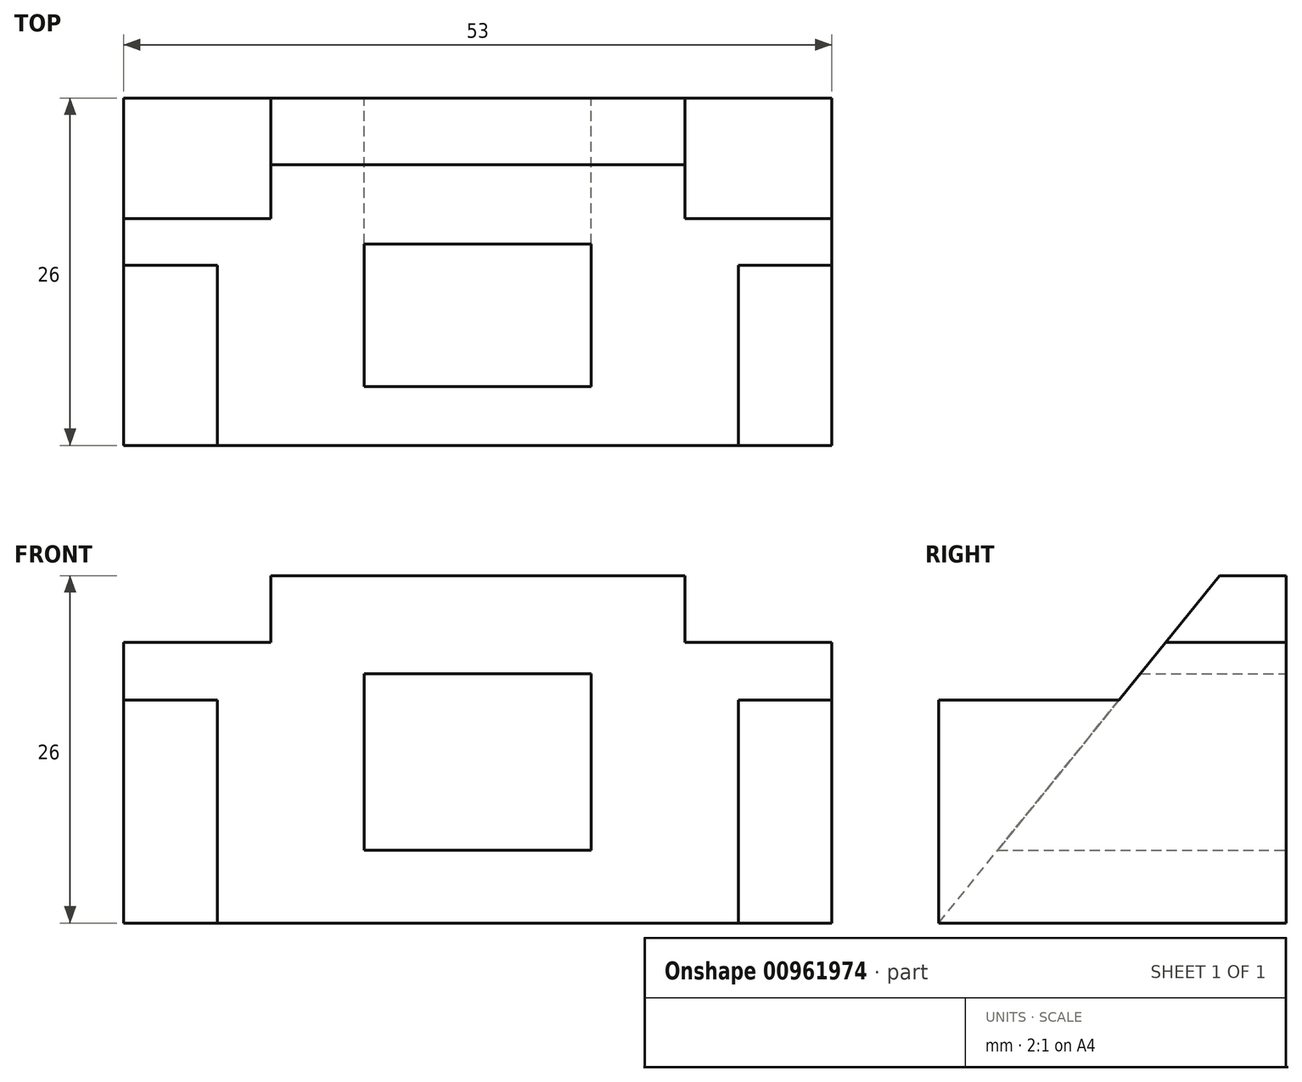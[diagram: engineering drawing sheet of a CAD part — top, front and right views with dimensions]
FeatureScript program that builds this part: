
annotation { "Feature Type Name" : "Feature", "Feature Type Description" : "" }
export const myFeature = defineFeature(function(context is Context, id is Id, definition is map)
    precondition{}
    {
        {
            var Q0;
            Q0=qCreatedBy(makeId("Top.planeOp"),FACE);
            var sketch = newSketch(context, id + "F0", { "sketchPlane" : qUnion([Q0])});
            skLineSegment(sketch, "E0.bottom", {"start": v(0, 0) * mm, "end": v(53, 0) * mm});
            skLineSegment(sketch, "E0.top", {"start": v(0, 26) * mm, "end": v(53, 26) * mm});
            skLineSegment(sketch, "E0.left", {"start": v(0, 0) * mm, "end": v(0, 26) * mm});
            skLineSegment(sketch, "E0.right", {"start": v(53, 0) * mm, "end": v(53, 26) * mm});
            skSolve(sketch);
        }
        {
            var Q0;
            Q0=makeQuery(id+"F0.imprint","IMPRINT",FACE,{"disambiguationData":[TD([[makeQuery(id+"F0.imprint","IMPRINT",EDGE,{"derivedFrom":sQuery(id+"F0.wireOp",EDGE,"E0.bottom")}),1.0]])]});
            extrude(context, id + "F1", {"entities" : qUnion([Q0]), "depth" : 26 * mm, "offsetDistance" : 25 * mm});
        }
        {
            var Q0;
            Q0=makeQuery(id+"F1.opExtrude","SWEPT_FACE",FACE,{"disambiguationData":[OSD([sQuery(id+"F0.wireOp",EDGE,"E0.right")])]});
            cPlane(context, id + "F2", {"entities" : qUnion([Q0]), "cplaneType" : CPlaneType.OFFSET, "offset" : 7 * mm, "oppositeDirection" : true, "width" : 150 * mm, "height" : 150 * mm});
        }
        {
            var Q0;
            Q0=qCreatedBy(id+"F2.planeOp",FACE);
            var sketch = newSketch(context, id + "F3", { "sketchPlane" : qUnion([Q0])});
            skLineSegment(sketch, "E1.0", {"start": v(0, 26) * mm, "end": v(26, 26) * mm});
            skPoint(sketch, "E2.0", {"position": v(0, 0) * mm});
            skLineSegment(sketch, "E3", {"start": v(0, 0) * mm, "end": v(21, 26) * mm});
            skLineSegment(sketch, "E4", {"start": v(0, 26) * mm, "end": v(0, 0) * mm});
            skSolve(sketch);
        }
        {
            var Q0;
            Q0 = qSketchRegion(id + "F3", true);
            extrude(context, id + "F4", {"entities" : qUnion([Q0]), "operationType" : NewBodyOperationType.REMOVE, "oppositeDirection" : true, "depth" : 39 * mm, "offsetDistance" : 25 * mm});
        }
        {
            var Q0;
            Q0=makeQuery(id+"F1.opExtrude","SWEPT_FACE",FACE,{"disambiguationData":[OSD([sQuery(id+"F0.wireOp",EDGE,"E0.right")])]});
            var sketch = newSketch(context, id + "F5", { "sketchPlane" : qUnion([Q0])});
            skLineSegment(sketch, "E5.0", {"start": v(0, 26) * mm, "end": v(26, 26) * mm});
            skLineSegment(sketch, "E6.0", {"start": v(26, 26) * mm, "end": v(26, 0) * mm});
            skLineSegment(sketch, "E7.0", {"start": v(0, 0) * mm, "end": v(26, 0) * mm});
            skLineSegment(sketch, "E8.0", {"start": v(0, 26) * mm, "end": v(0, 0) * mm});
            skLineSegment(sketch, "E9", {"start": v(26, 21) * mm, "end": v(16.96, 21) * mm});
            skLineSegment(sketch, "E10", {"start": v(13.49, 16.7) * mm, "end": v(0, 16.7) * mm});
            skLineSegment(sketch, "E11.0", {"start": v(13.49, 16.7) * mm, "end": v(16.96, 21) * mm});
            skPoint(sketch, "E12.orphan", {"position": v(21, 26) * mm});
            skPoint(sketch, "E13.orphan", {"position": v(0, 0) * mm});
            skSolve(sketch);
        }
        {
            var Q0;
            {var subQ1=sQuery(id+"F5.wireOp",EDGE,"E5.0");Q0=makeQuery(id+"F5.imprint","IMPRINT",FACE,{"disambiguationData":[TD([[makeQuery(id+"F5.imprint","IMPRINT",EDGE,{"derivedFrom":subQ1}),-1.0]])]});}
            extrude(context, id + "F6", {"entities" : qUnion([Q0]), "operationType" : NewBodyOperationType.REMOVE, "oppositeDirection" : true, "depth" : 11 * mm, "offsetDistance" : 25 * mm});
        }
        {
            var Q0;
            Q0=makeQuery(id+"F1.opExtrude","SWEPT_FACE",FACE,{"disambiguationData":[OSD([sQuery(id+"F0.wireOp",EDGE,"E0.left")])]});
            var sketch = newSketch(context, id + "F7", { "sketchPlane" : qUnion([Q0])});
            skLineSegment(sketch, "E14.0.0", {"start": v(-16.96, 21) * mm, "end": v(-13.49, 16.7) * mm});
            skLineSegment(sketch, "E14.0.1", {"start": v(-13.49, 16.7) * mm, "end": v(0, 16.7) * mm});
            skLineSegment(sketch, "E14.0.2", {"start": v(0, 16.7) * mm, "end": v(0, 0) * mm});
            skLineSegment(sketch, "E14.0.3", {"start": v(0, 0) * mm, "end": v(-26, 0) * mm});
            skLineSegment(sketch, "E14.0.4", {"start": v(-26, 0) * mm, "end": v(-26, 21) * mm});
            skLineSegment(sketch, "E14.0.5", {"start": v(-26, 21) * mm, "end": v(-16.96, 21) * mm});
            skLineSegment(sketch, "E15.0", {"start": v(-26, 26) * mm, "end": v(-26, 0) * mm});
            skLineSegment(sketch, "E16.0", {"start": v(0, 26) * mm, "end": v(-26, 26) * mm});
            skLineSegment(sketch, "E17.0", {"start": v(0, 26) * mm, "end": v(0, 0) * mm});
            skSolve(sketch);
        }
        {
            var Q0;
            Q0=makeQuery(id+"F7.imprint","IMPRINT",FACE,{"disambiguationData":[TD([[makeQuery(id+"F7.imprint","IMPRINT",EDGE,{"derivedFrom":sQuery(id+"F7.wireOp",EDGE,"E14.0.0")}),1.0]])]});
            extrude(context, id + "F8", {"entities" : qUnion([Q0]), "operationType" : NewBodyOperationType.REMOVE, "oppositeDirection" : true, "depth" : 11 * mm, "offsetDistance" : 25 * mm});
        }
        {
            var Q0;
            Q0=makeQuery(id+"F8.boolean.opBoolean","MERGE",FACE,{"derivedFrom":[makeQuery(id+"F6.boolean.opBoolean","MERGE",FACE,{"derivedFrom":[makeQuery(id+"F4.boolean.opBoolean","COPY",FACE,{"derivedFrom":makeQuery(id+"F4.opExtrude","SWEPT_FACE",FACE,{"disambiguationData":[OSD([sQuery(id+"F3.wireOp",EDGE,"E3")])]})})],"fromTools":[makeQuery(id+"F6.opExtrude","SWEPT_FACE",FACE,{"disambiguationData":[OSD([sQuery(id+"F5.wireOp",EDGE,"E11.0")])]})]})],"fromTools":[makeQuery(id+"F8.opExtrude","SWEPT_FACE",FACE,{"disambiguationData":[OSD([sQuery(id+"F7.wireOp",EDGE,"E14.0.0")])]})]});
            var sketch = newSketch(context, id + "F9", { "sketchPlane" : qUnion([Q0])});
            skLineSegment(sketch, "E18.bottom", {"start": v(18, 24) * mm, "end": v(35, 24) * mm});
            skLineSegment(sketch, "E18.top", {"start": v(18, 7) * mm, "end": v(35, 7) * mm});
            skLineSegment(sketch, "E18.left", {"start": v(18, 24) * mm, "end": v(18, 7) * mm});
            skLineSegment(sketch, "E18.right", {"start": v(35, 24) * mm, "end": v(35, 7) * mm});
            skSolve(sketch);
        }
        {
            var Q0;
            Q0=makeQuery(id+"F1.opExtrude","SWEPT_FACE",FACE,{"disambiguationData":[OSD([sQuery(id+"F0.wireOp",EDGE,"E0.top")])]});
            var sketch = newSketch(context, id + "F10", { "sketchPlane" : qUnion([Q0])});
            skLineSegment(sketch, "E19.0", {"start": v(-18, 18.67) * mm, "end": v(-35, 18.67) * mm});
            skLineSegment(sketch, "E20.0", {"start": v(-18, 18.67) * mm, "end": v(-18, 5.45) * mm});
            skLineSegment(sketch, "E21.0", {"start": v(-18, 5.45) * mm, "end": v(-35, 5.45) * mm});
            skLineSegment(sketch, "E22.0", {"start": v(-35, 18.67) * mm, "end": v(-35, 5.45) * mm});
            skSolve(sketch);
        }
        {
            var Q1;
            Q1=makeQuery(id+"F9.imprint","IMPRINT",FACE,{"disambiguationData":[TD([[makeQuery(id+"F9.imprint","IMPRINT",EDGE,{"derivedFrom":sQuery(id+"F9.wireOp",EDGE,"E18.bottom")}),-1.0]])]});
            var Q2;
            Q2=makeQuery(id+"F10.imprint","IMPRINT",FACE,{"disambiguationData":[TD([[makeQuery(id+"F10.imprint","IMPRINT",EDGE,{"derivedFrom":sQuery(id+"F10.wireOp",EDGE,"E19.0")}),1.0]])]});
            loft(context, id + "F11", {"operationType" : NewBodyOperationType.REMOVE, "sheetProfilesArray" : [{ "sheetProfileEntities" : qUnion([Q1]) }, { "sheetProfileEntities" : qUnion([Q2]) }]});
        }
    });
